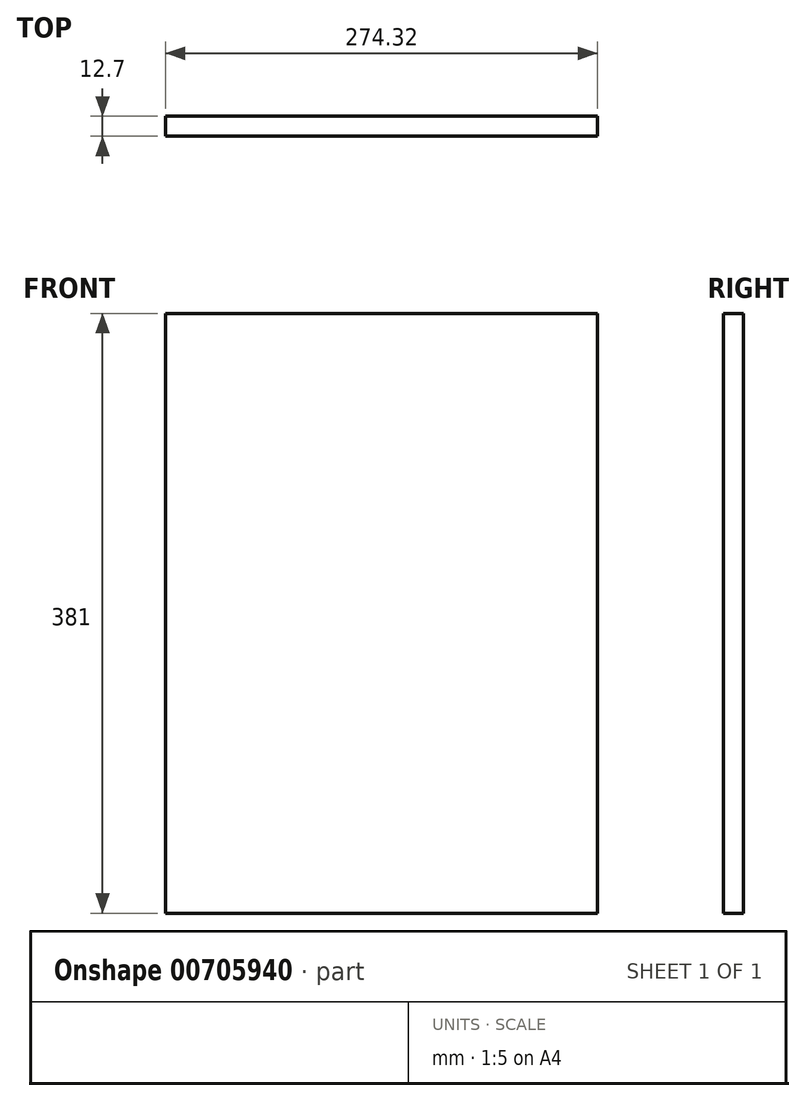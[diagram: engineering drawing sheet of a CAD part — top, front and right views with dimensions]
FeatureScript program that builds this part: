
annotation { "Feature Type Name" : "Feature", "Feature Type Description" : "" }
export const myFeature = defineFeature(function(context is Context, id is Id, definition is map)
    precondition{}
    {
        {
            var Q0;
            Q0=qCreatedBy(makeId("Front.planeOp"),FACE);
            var sketch = newSketch(context, id + "F0", { "sketchPlane" : qUnion([Q0])});
            skLineSegment(sketch, "E0.bottom", {"start": v(-143.47, 180.99) * mm, "end": v(130.85, 180.99) * mm});
            skLineSegment(sketch, "E0.top", {"start": v(-143.47, -200.01) * mm, "end": v(130.85, -200.01) * mm});
            skLineSegment(sketch, "E0.left", {"start": v(-143.47, 180.99) * mm, "end": v(-143.47, -200.01) * mm});
            skLineSegment(sketch, "E0.right", {"start": v(130.85, 180.99) * mm, "end": v(130.85, -200.01) * mm});
            skSolve(sketch);
        }
        {
            var Q0;
            Q0=makeQuery(id+"F0.imprint","IMPRINT",FACE,{"disambiguationData":[TD([[makeQuery(id+"F0.imprint","IMPRINT",EDGE,{"derivedFrom":sQuery(id+"F0.wireOp",EDGE,"E0.bottom")}),-1.0]])]});
            extrude(context, id + "F1", {"entities" : qUnion([Q0]), "depth" : 12.7 * mm, "offsetDistance" : 25.4 * mm});
        }
    });
